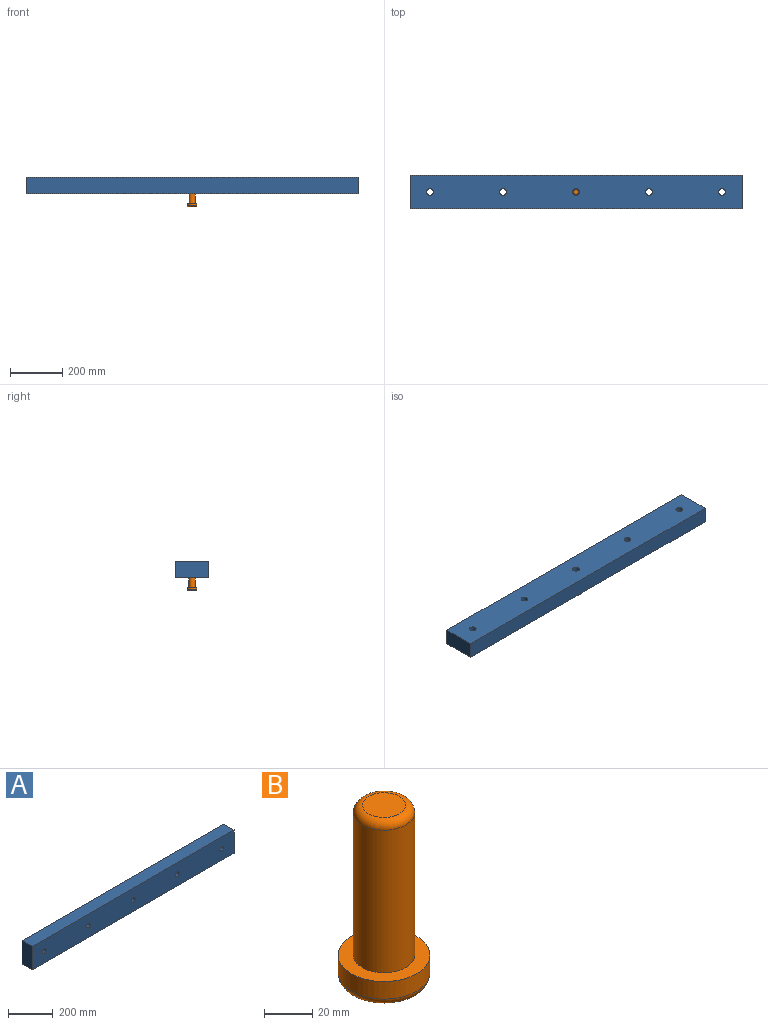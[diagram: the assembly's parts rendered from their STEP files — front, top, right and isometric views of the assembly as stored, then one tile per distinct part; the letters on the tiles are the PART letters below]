
ASSEMBLY  parts=2 mates=1
PART A: 11 faces, bbox 1270x63.5x127 mm
  f0: plane 127x63.5mm, normal (-1,0,0), area 8064.5mm2, adj f1,f3,f4,f5
  f1: plane 1270x63.5mm, normal (0,0,-1), area 80645mm2, adj f0,f2,f4,f5
  f2: plane 127x63.5mm, normal (1,0,0), area 8064.5mm2, adj f1,f3,f4,f5
  f3: plane 1270x63.5mm, normal (0,0,1), area 80645mm2, adj f0,f2,f4,f5
  f4: plane 1270x127mm, normal (0,-1,0), area 158756.5mm2, adj f0,f1,f2,f3,f6,f7,f8,f9
  f5: plane 1270x127mm, normal (0,1,0), area 158756.5mm2, adj f0,f1,f2,f3,f6,f7,f8,f9
  f6: cylinder r=12.7mm len=63.5mm, axis (0,1,0), area 5067.1mm2, adj f4,f5
  f7: cylinder r=12.7mm len=63.5mm, axis (0,1,0), area 5067.1mm2, adj f4,f5
  f8: cylinder r=12.7mm len=63.5mm, axis (0,1,0), area 5067.1mm2, adj f4,f5
  f9: cylinder r=12.7mm len=63.5mm, axis (0,1,0), area 5067.1mm2, adj f4,f5
  f10: cylinder r=12.7mm len=63.5mm, axis (0,1,0), area 5067.1mm2, adj f4,f5
PART B: 7 faces, bbox 41.2x41.2x88.9 mm
  f0: cylinder r=12.7mm len=72.39mm, axis (0,0,-1), area 5776.5mm2, adj f2,f5
  f1: plane 17.78x17.78mm, normal (0,0,1), area 248.3mm2, adj f2
  f2: torus R=8.89mm, axis (0,0,1), area 425.5mm2, adj f0,f1
  f3: cylinder r=19.05mm len=38.1mm, axis (0,0,1), area 1064.1mm2, adj f5,f6
  f4: plane 30.48x30.48mm, normal (0,0,-1), area 729.7mm2, adj f6
  f5: plane 38.1x38.1mm, normal (0,0,1), area 633.4mm2, adj f0,f3
  f6: torus R=15.24mm, axis (0,0,1), area 664.3mm2, adj f3,f4
PLACE A rot(axis=(-1,0,0),90deg) t=(-42.23,-5.78,48.48)mm
PLACE B t=(-42.23,-5.78,12.28)mm
MATE pin_slot A.f8 <-> B.f0  axis (0,0,-1) through (-42.23,-5.78,48.48)mm
